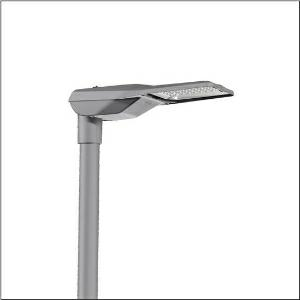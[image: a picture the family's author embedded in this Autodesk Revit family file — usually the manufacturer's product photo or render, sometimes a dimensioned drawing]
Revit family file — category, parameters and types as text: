
# Revit family: streetlight_sl_21_iq_mini___st1_0a_5xe2d31v08jb_ee78
name_source: partatom
category: Lighting Fixtures
units: mm (PartAtom-declared; Revit-internal decimal feet)

## family parameters
Cut with Voids When Loaded = No
Host = Face
Light Source = No
Part Type = Normal
Room Calculation Point = No
Round Connector Dimension = Use Diameter
Shared = No

## types (1)
- --- (1 x LED, 11210 lm, 72.5 W, 3000K)
    Apparent Load = 73 VA
    CIE Flux Codes = 40 73 97 100 100
    Color Rendering = 70
    Color Temperature = 3000K
    Default Elevation = 1800 mm
    Description = Streetlight SL 21 iQ mini, mast luminaire, primary light control with lens, of PMMA, primary optical cover: cover, of toughened safety glass, transparent, light distribution: ST1.0a, light emission: direct distribution, primary light characteristic: asymmetric, installation type: post-top, side-entry, LED, High Power LED, rated luminous flux: 11.210lm, luminous efficacy: 155lm/W, light colour: 730, colour temperature: 3000K, control gear: iQ-Street Remote, D4i with power reduction, control: pre-setting: logarithmic dimming characteristic, Street-Remote, Auto-Match, Temp-Guard, Lumen-Switch, Night-Set, Smart-Wire, Light-Fading, Desk-Remote (wireless, voltage-free reading and setting of iQ features in the workshop via application-optimized NFC function/RFID function), optimised constant luminous flux control (CLO 2.0), mains connection: 220..240V, AC, 50/60Hz, start of lifetime: 73W, end of service life: 76W, reduction: 33W, luminaire housing, of diecast aluminium, powder-coated, SITECO metallic grey (DB 702S), corrosivity category C5 high according to DIN EN ISO 12944, please order mast flange separately, inclination adjustable: 0°, 5°, 10°, 15°, sealing non-destructively replaceable, multi-level sealing system, length: 628mm, width: 235mm, height: 110mm, mast flange for spigot size: 42mm (side-entry): 5XC10008XM4, 60/48mm (side-entry/post-top): 5XC10108XM2, 76/60mm (side-entry/post-top): 5XC10108XM1, mounting height: 4..8m, Smart Interface above, protection rating (complete): IP66, insulation class (complete): insulation class II (safety insulation), certification: CE, ENEC, ENEC+, VDE, impact resistance: IK10, permissible operating ambient temperature for outdoor applications: -40..+50°C, standard-compliant lighting for roads and squares, packaging unit: 1 piece

Light Distribution: ST1.0a
    Height = 110 mm
    Lamp = 1 x LED
    Lamp Light Flux = 11210 lm
    Lamp Power = 72.5 W
    Lamp count = 1
    Length = 625 mm
    Luminous efficacy = 155 lm/W
    Manufacturer = Siteco
    ModVariant = No
    Model = 5XE2D31V08JB
    Number of Poles = 1
    OnlyDefault = Yes
    Power Factor = 1
    Product Name = Streetlight SL 21 iQ mini | ST1.0a
    Product group = mast luminaire | pylon top
    ProductGroupID = 6100
    Protection Class = Protection class II
    Protection Degree = IP 66
    RLX_Detail_Level = 1
    RLX_Emergency_Light_Flux = 0 lm
    RLX_Emergency_Type = 0
    RLX_Emergency_Type_DB = No
    RlxData = <blob elided: 93273 chars, md5=6910da48>
    Socket = socket
    Standby Power = 0 W
    System Light Flux = 11210 lm
    System Power = 73 W
    Type Comments = factory setting: luminous flux: 100 % | dim-lin: 254 | 755 mA
    Type Image = l_1003515.jpg
    URL = http://relux.com
    VarID = @adj_114309
    Voltage = 0 V
    Weight = 0.00 kg
    Width = 234 mm

## geometry (parser evidence)
native form markers: Blend x4, Sweep x10
no freeform markers — native parametric forms only
